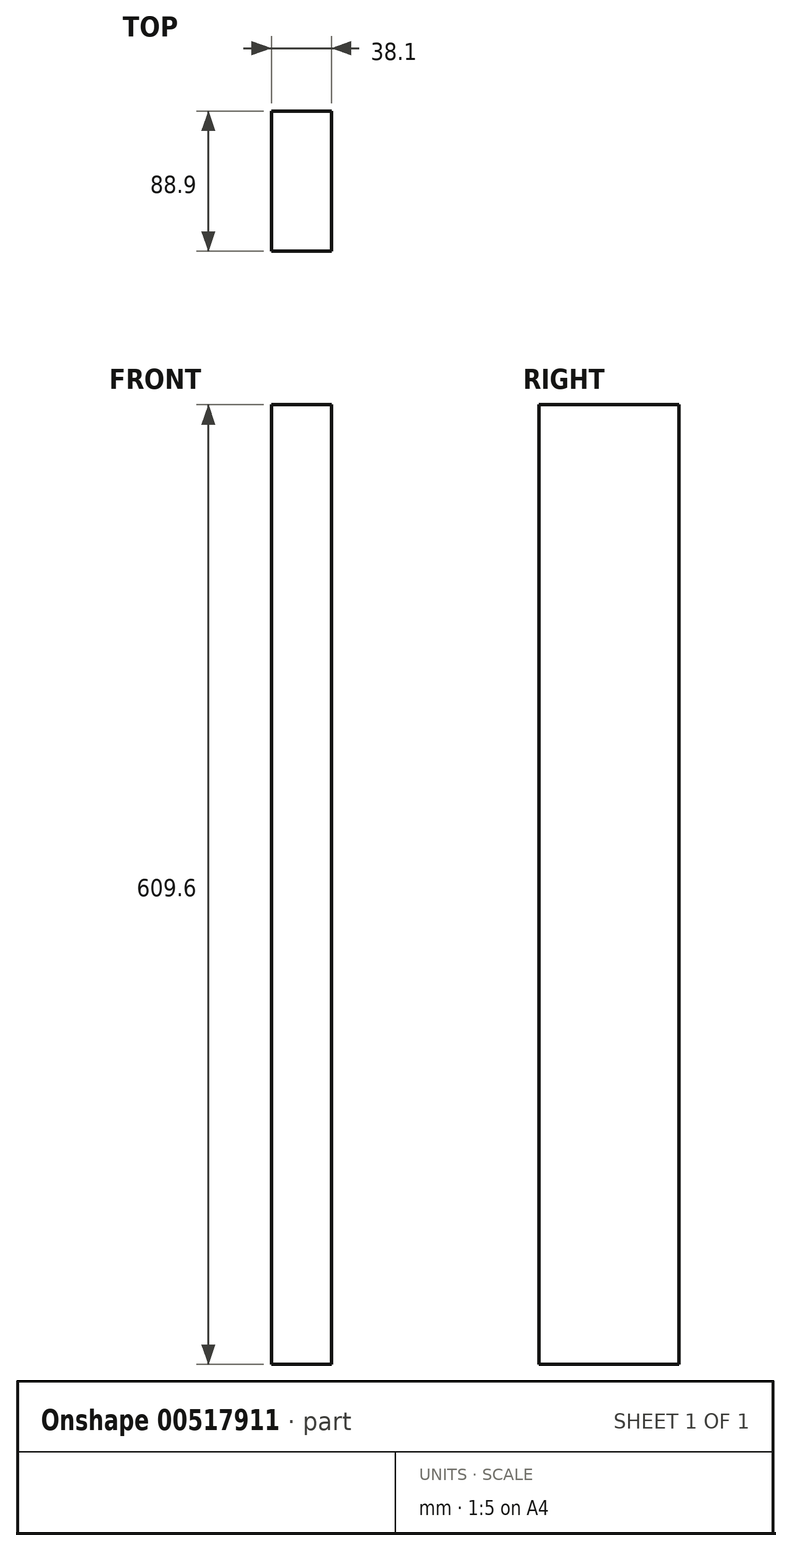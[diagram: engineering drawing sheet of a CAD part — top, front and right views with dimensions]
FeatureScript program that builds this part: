
annotation { "Feature Type Name" : "Feature", "Feature Type Description" : "" }
export const myFeature = defineFeature(function(context is Context, id is Id, definition is map)
    precondition{}
    {
        {
            var Q0;
            Q0=qCreatedBy(makeId("Top.planeOp"),FACE);
            var sketch = newSketch(context, id + "F0", { "sketchPlane" : qUnion([Q0])});
            skLineSegment(sketch, "E0.bottom", {"start": v(19.05, 44.45) * mm, "end": v(-19.05, 44.45) * mm});
            skLineSegment(sketch, "E0.top", {"start": v(19.05, -44.45) * mm, "end": v(-19.05, -44.45) * mm});
            skLineSegment(sketch, "E0.left", {"start": v(19.05, 44.45) * mm, "end": v(19.05, -44.45) * mm});
            skLineSegment(sketch, "E0.right", {"start": v(-19.05, 44.45) * mm, "end": v(-19.05, -44.45) * mm});
            skPoint(sketch, "E0.middle", {"position": v(0, 0) * mm});
            skSolve(sketch);
        }
        {
            var Q0;
            Q0=makeQuery(id+"F0.imprint","IMPRINT",FACE,{"disambiguationData":[TD([[makeQuery(id+"F0.imprint","IMPRINT",EDGE,{"derivedFrom":sQuery(id+"F0.wireOp",EDGE,"E0.bottom")}),1.0]])]});
            extrude(context, id + "F1", {"entities" : qUnion([Q0]), "endBound" : BoundingType.SYMMETRIC, "depth" : 609.6 * mm, "offsetDistance" : 25.4 * mm});
        }
    });
